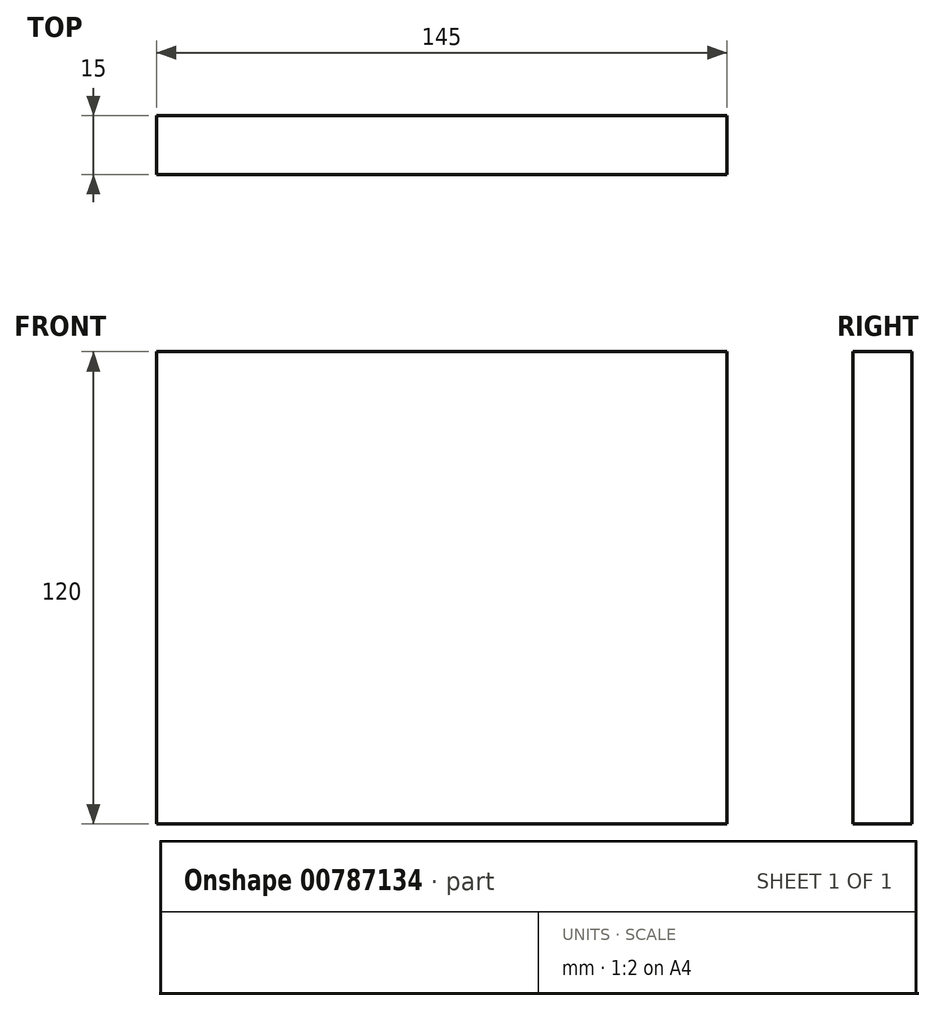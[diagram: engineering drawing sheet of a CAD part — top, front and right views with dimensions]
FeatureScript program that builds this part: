
annotation { "Feature Type Name" : "Feature", "Feature Type Description" : "" }
export const myFeature = defineFeature(function(context is Context, id is Id, definition is map)
    precondition{}
    {
        {
            var Q0;
            Q0=qCreatedBy(makeId("Front.planeOp"),FACE);
            var sketch = newSketch(context, id + "F0", { "sketchPlane" : qUnion([Q0])});
            skLineSegment(sketch, "E0.bottom", {"start": v(72.5, -60) * mm, "end": v(-72.5, -60) * mm});
            skLineSegment(sketch, "E0.top", {"start": v(72.5, 60) * mm, "end": v(-72.5, 60) * mm});
            skLineSegment(sketch, "E0.left", {"start": v(72.5, -60) * mm, "end": v(72.5, 60) * mm});
            skLineSegment(sketch, "E0.right", {"start": v(-72.5, -60) * mm, "end": v(-72.5, 60) * mm});
            skPoint(sketch, "E0.middle", {"position": v(0, 0) * mm});
            skSolve(sketch);
        }
        {
            var Q0;
            Q0=makeQuery(id+"F0.imprint","IMPRINT",FACE,{"disambiguationData":[TD([[makeQuery(id+"F0.imprint","IMPRINT",EDGE,{"derivedFrom":sQuery(id+"F0.wireOp",EDGE,"E0.bottom")}),-1.0]])]});
            extrude(context, id + "F1", {"entities" : qUnion([Q0]), "depth" : 15 * mm, "offsetDistance" : 25 * mm});
        }
    });
